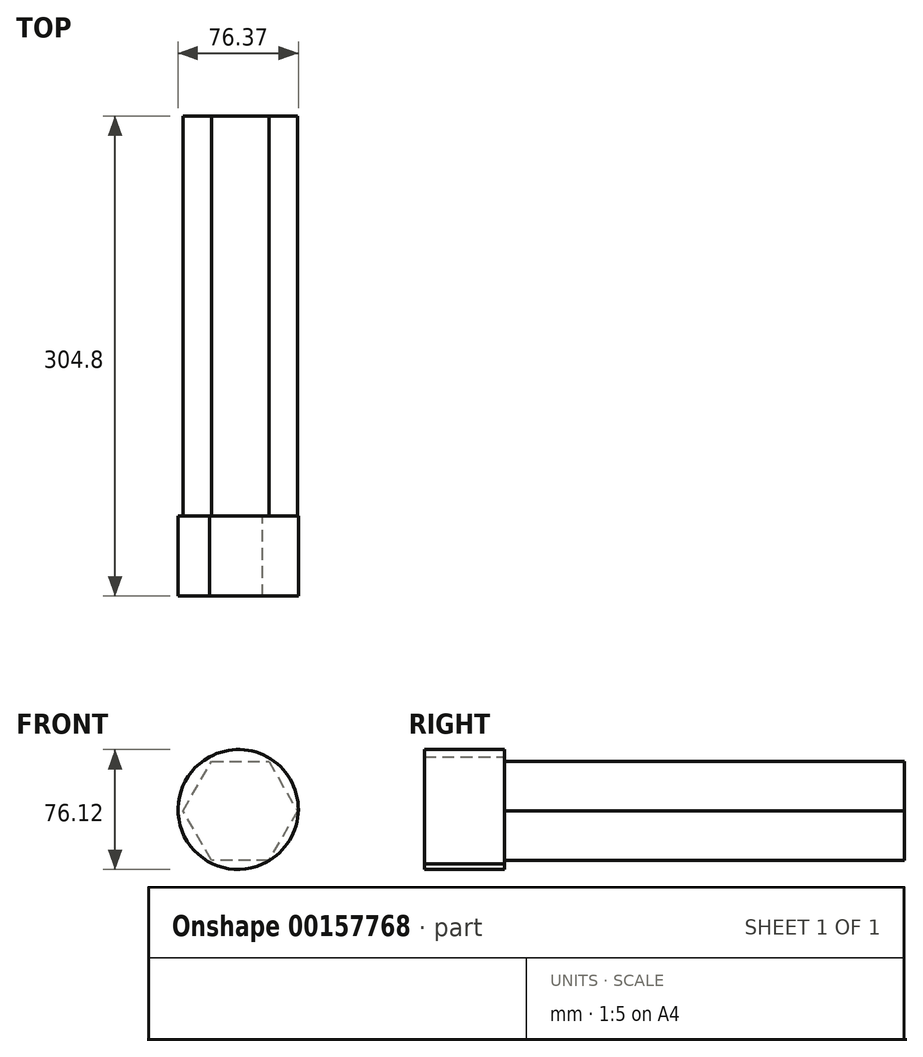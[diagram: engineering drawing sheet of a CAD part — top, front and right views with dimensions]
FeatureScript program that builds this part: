
annotation { "Feature Type Name" : "Feature", "Feature Type Description" : "" }
export const myFeature = defineFeature(function(context is Context, id is Id, definition is map)
    precondition{}
    {
        {
            var Q0;
            Q0=qCreatedBy(makeId("Front.planeOp"),FACE);
            var sketch = newSketch(context, id + "F0", { "sketchPlane" : qUnion([Q0])});
            skCircle(sketch, "E0.cCircle", {"center": v(-42.15, 31.57) * mm, "radius": 31.47 * mm, "construction": true});
            skLineSegment(sketch, "E0.0", {"start": v(-5.8, 31.46) * mm, "end": v(-24.07, 0.04) * mm});
            skLineSegment(sketch, "E0.1", {"start": v(-24.07, 0.04) * mm, "end": v(-60.41, 0.15) * mm});
            skLineSegment(sketch, "E0.2", {"start": v(-60.41, 0.15) * mm, "end": v(-78.5, 31.67) * mm});
            skLineSegment(sketch, "E0.3", {"start": v(-78.5, 31.67) * mm, "end": v(-60.23, 63.1) * mm});
            skLineSegment(sketch, "E0.4", {"start": v(-60.23, 63.1) * mm, "end": v(-23.88, 62.99) * mm});
            skLineSegment(sketch, "E0.5", {"start": v(-23.88, 62.99) * mm, "end": v(-5.8, 31.46) * mm});
            skPoint(sketch, "E0.0.midPoint", {"position": v(-14.94, 15.75) * mm});
            skSolve(sketch);
        }
        {
            var Q0;
            Q0=makeQuery(id+"F0.imprint","IMPRINT",FACE,{"disambiguationData":[TD([[makeQuery(id+"F0.imprint","IMPRINT",EDGE,{"derivedFrom":sQuery(id+"F0.wireOp",EDGE,"E0.0")}),-1.0]])]});
            extrude(context, id + "F1", {"entities" : qUnion([Q0]), "depth" : 25.4 * mm});
        }
        {
            var Q0;
            Q0=makeQuery(id+"F1.opExtrude","CAP_FACE",FACE,{"disambiguationData":[OSD([sQuery(id+"F0.wireOp",EDGE,"E0.0"),sQuery(id+"F0.wireOp",EDGE,"E0.1"),sQuery(id+"F0.wireOp",EDGE,"E0.2"),sQuery(id+"F0.wireOp",EDGE,"E0.3"),sQuery(id+"F0.wireOp",EDGE,"E0.4"),sQuery(id+"F0.wireOp",EDGE,"E0.5")])],"isStart":true});
            var Q1;
            Q1=makeQuery(id+"F1.opExtrude","CAP_FACE",FACE,{"disambiguationData":[OSD([sQuery(id+"F0.wireOp",EDGE,"E0.0"),sQuery(id+"F0.wireOp",EDGE,"E0.1"),sQuery(id+"F0.wireOp",EDGE,"E0.2"),sQuery(id+"F0.wireOp",EDGE,"E0.3"),sQuery(id+"F0.wireOp",EDGE,"E0.4"),sQuery(id+"F0.wireOp",EDGE,"E0.5")])],"isStart":false});
            extrude(context, id + "F2", {"entities" : qUnion([Q0, Q1]), "operationType" : NewBodyOperationType.ADD, "depth" : 127 * mm});
        }
        {
            var Q0;
            Q0=qCreatedBy(makeId("Front.planeOp"),FACE);
            var sketch = newSketch(context, id + "F3", { "sketchPlane" : qUnion([Q0])});
            skCircle(sketch, "E1", {"center": v(-43.14, 32.62) * mm, "radius": 37.94 * mm});
            skSolve(sketch);
        }
        {
            var Q0;
            Q0 = qSketchRegion(id + "F3", true);
            extrude(context, id + "F4", {"entities" : qUnion([Q0]), "operationType" : NewBodyOperationType.ADD, "depth" : 50.8 * mm});
        }
        {
            var Q0;
            {var subQ0=sQuery(id+"F0.wireOp",EDGE,"E0.5");var subQ1=sQuery(id+"F0.wireOp",EDGE,"E0.4");var subQ2=sQuery(id+"F0.wireOp",EDGE,"E0.3");var subQ3=sQuery(id+"F0.wireOp",EDGE,"E0.2");var subQ4=sQuery(id+"F0.wireOp",EDGE,"E0.1");var subQ5=sQuery(id+"F0.wireOp",EDGE,"E0.0");Q0=makeQuery(id+"F2.opExtrude","CAP_FACE",FACE,{"disambiguationData":[OSD([subQ5,subQ4,subQ3,subQ2,subQ1,subQ0]),TDD([makeQuery(id+"F1.opExtrude","CAP_FACE",FACE,{"disambiguationData":[OSD([subQ5,subQ4,subQ3,subQ2,subQ1,subQ0])],"isStart":true})])],"isStart":false});}
            extrude(context, id + "F5", {"entities" : qUnion([Q0]), "operationType" : NewBodyOperationType.ADD, "depth" : 127 * mm});
        }
        {
            var Q0;
            Q0=qCreatedBy(makeId("Front.planeOp"),FACE);
            var sketch = newSketch(context, id + "F6", { "sketchPlane" : qUnion([Q0])});
            skCircle(sketch, "E2", {"center": v(-43.65, 32.36) * mm, "radius": 37.92 * mm});
            skPoint(sketch, "E2.first.point", {"position": v(-42.6, 70.26) * mm});
            skPoint(sketch, "E2.second.point", {"position": v(-43.74, -5.56) * mm});
            skPoint(sketch, "E2.third.point", {"position": v(-5.83, 29.7) * mm});
            skSolve(sketch);
        }
        {
            var Q0;
            Q0 = qSketchRegion(id + "F6", true);
            extrude(context, id + "F7", {"entities" : qUnion([Q0]), "operationType" : NewBodyOperationType.ADD, "depth" : 50.8 * mm});
        }
    });
